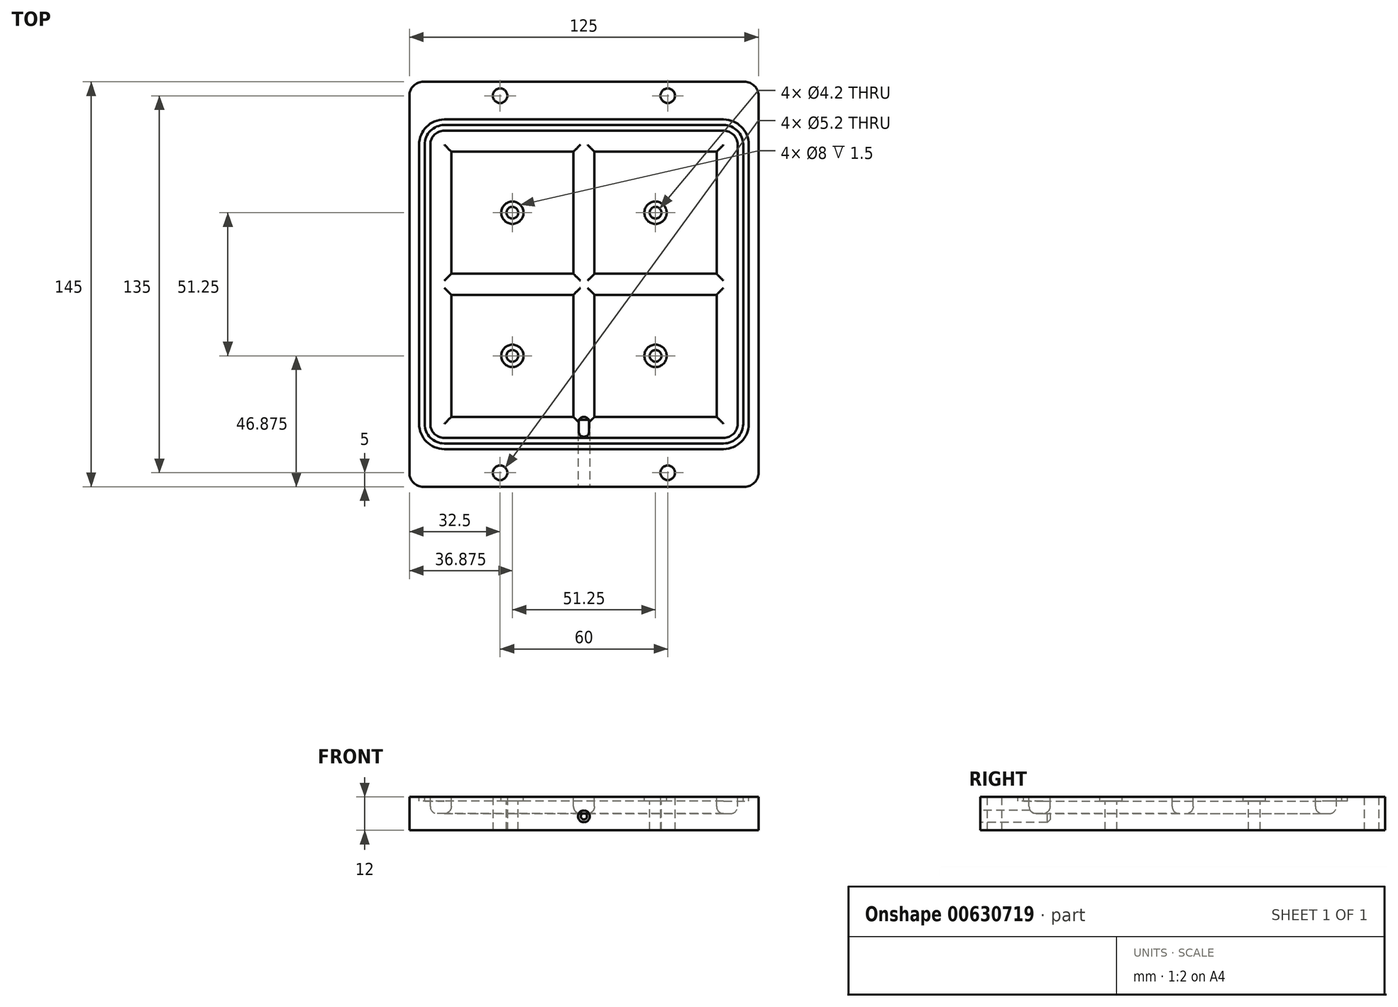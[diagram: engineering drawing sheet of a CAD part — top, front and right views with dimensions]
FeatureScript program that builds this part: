
annotation { "Feature Type Name" : "Feature", "Feature Type Description" : "" }
export const myFeature = defineFeature(function(context is Context, id is Id, definition is map)
    precondition{}
    {
        {
            var Q0;
            Q0=qCreatedBy(makeId("Top.planeOp"),FACE);
            var sketch = newSketch(context, id + "F0", { "sketchPlane" : qUnion([Q0])});
            skLineSegment(sketch, "E0.bottom", {"start": v(52.5, -62.5) * mm, "end": v(-52.5, -62.5) * mm, "construction": true});
            skLineSegment(sketch, "E0.top", {"start": v(52.5, 62.5) * mm, "end": v(-52.5, 62.5) * mm, "construction": true});
            skLineSegment(sketch, "E0.left", {"start": v(62.5, -52.5) * mm, "end": v(62.5, 52.5) * mm, "construction": true});
            skLineSegment(sketch, "E0.right", {"start": v(-62.5, -52.5) * mm, "end": v(-62.5, 52.5) * mm, "construction": true});
            skPoint(sketch, "E0.middle", {"position": v(0, 0) * mm});
            skPoint(sketch, "E1.visualSharp", {"position": v(-62.5, 62.5) * mm});
            skArc(sketch, "E1.filletArc", {"start": v(-52.5, 62.5) * mm, "mid": v(-59.57, 59.57) * mm, "end": v(-62.5, 52.5) * mm, "construction": true});
            skPoint(sketch, "E2.visualSharp", {"position": v(62.5, 62.5) * mm});
            skArc(sketch, "E2.filletArc", {"start": v(62.5, 52.5) * mm, "mid": v(59.57, 59.57) * mm, "end": v(52.5, 62.5) * mm, "construction": true});
            skPoint(sketch, "E3.visualSharp", {"position": v(62.5, -62.5) * mm});
            skArc(sketch, "E3.filletArc", {"start": v(52.5, -62.5) * mm, "mid": v(59.57, -59.57) * mm, "end": v(62.5, -52.5) * mm, "construction": true});
            skPoint(sketch, "E4.visualSharp", {"position": v(-62.5, -62.5) * mm});
            skArc(sketch, "E4.filletArc", {"start": v(-62.5, -52.5) * mm, "mid": v(-59.57, -59.57) * mm, "end": v(-52.5, -62.5) * mm, "construction": true});
            skSolve(sketch);
        }
        {
            var Q0;
            Q0=qCreatedBy(makeId("Top.planeOp"),FACE);
            var sketch = newSketch(context, id + "F1", { "sketchPlane" : qUnion([Q0])});
            skLineSegment(sketch, "E5.bottom", {"start": v(57.5, -72.5) * mm, "end": v(-57.5, -72.5) * mm});
            skLineSegment(sketch, "E5.top", {"start": v(57.5, 72.5) * mm, "end": v(-57.5, 72.5) * mm});
            skLineSegment(sketch, "E5.left", {"start": v(62.5, -67.5) * mm, "end": v(62.5, 67.5) * mm});
            skLineSegment(sketch, "E5.right", {"start": v(-62.5, -67.5) * mm, "end": v(-62.5, 67.5) * mm});
            skPoint(sketch, "E5.middle", {"position": v(0, 0) * mm});
            skPoint(sketch, "E6.visualSharp", {"position": v(-62.5, 72.5) * mm});
            skArc(sketch, "E6.filletArc", {"start": v(-57.5, 72.5) * mm, "mid": v(-61.04, 71.04) * mm, "end": v(-62.5, 67.5) * mm});
            skPoint(sketch, "E7.visualSharp", {"position": v(62.5, 72.5) * mm});
            skArc(sketch, "E7.filletArc", {"start": v(62.5, 67.5) * mm, "mid": v(61.04, 71.04) * mm, "end": v(57.5, 72.5) * mm});
            skPoint(sketch, "E8.visualSharp", {"position": v(62.5, -72.5) * mm});
            skArc(sketch, "E8.filletArc", {"start": v(57.5, -72.5) * mm, "mid": v(61.04, -71.04) * mm, "end": v(62.5, -67.5) * mm});
            skPoint(sketch, "E9.visualSharp", {"position": v(-62.5, -72.5) * mm});
            skArc(sketch, "E9.filletArc", {"start": v(-62.5, -67.5) * mm, "mid": v(-61.04, -71.04) * mm, "end": v(-57.5, -72.5) * mm});
            skLineSegment(sketch, "E10", {"start": v(-62.5, 67.5) * mm, "end": v(52.45, 67.5) * mm, "construction": true});
            skLineSegment(sketch, "E11", {"start": v(-48.85, -67.5) * mm, "end": v(50.9, -67.5) * mm, "construction": true});
            skCircle(sketch, "E12", {"center": v(-30, 67.5) * mm, "radius": 2.6 * mm});
            skCircle(sketch, "E13", {"center": v(30, 67.5) * mm, "radius": 2.6 * mm});
            skCircle(sketch, "E14", {"center": v(-30, -67.5) * mm, "radius": 2.6 * mm});
            skCircle(sketch, "E15", {"center": v(30, -67.5) * mm, "radius": 2.6 * mm});
            skSolve(sketch);
        }
        {
            var Q0;
            Q0=makeQuery(id+"F1.imprint","IMPRINT",FACE,{"disambiguationData":[TD([[makeQuery(id+"F1.imprint","IMPRINT",EDGE,{"derivedFrom":sQuery(id+"F1.wireOp",EDGE,"E5.bottom")}),-1.0]])]});
            extrude(context, id + "F2", {"entities" : qUnion([Q0]), "depth" : 12 * mm, "offsetDistance" : 25 * mm});
        }
        {
            var Q0;
            Q0=makeQuery(id+"F2.opExtrude","CAP_FACE",FACE,{"disambiguationData":[OSD([sQuery(id+"F1.wireOp",EDGE,"E5.bottom"),sQuery(id+"F1.wireOp",EDGE,"E5.top"),sQuery(id+"F1.wireOp",EDGE,"E5.left"),sQuery(id+"F1.wireOp",EDGE,"E5.right"),sQuery(id+"F1.wireOp",EDGE,"E6.filletArc"),sQuery(id+"F1.wireOp",EDGE,"E7.filletArc"),sQuery(id+"F1.wireOp",EDGE,"E8.filletArc"),sQuery(id+"F1.wireOp",EDGE,"E9.filletArc"),sQuery(id+"F1.wireOp",EDGE,"E12"),sQuery(id+"F1.wireOp",EDGE,"E13"),sQuery(id+"F1.wireOp",EDGE,"E14"),sQuery(id+"F1.wireOp",EDGE,"E15")])],"isStart":false});
            var sketch = newSketch(context, id + "F3", { "sketchPlane" : qUnion([Q0])});
            skLineSegment(sketch, "E16.bottom", {"start": v(50, -55) * mm, "end": v(-50, -55) * mm});
            skLineSegment(sketch, "E16.top", {"start": v(50, 55) * mm, "end": v(-50, 55) * mm});
            skLineSegment(sketch, "E16.left", {"start": v(55, -50) * mm, "end": v(55, 50) * mm});
            skLineSegment(sketch, "E16.right", {"start": v(-55, -50) * mm, "end": v(-55, 50) * mm});
            skPoint(sketch, "E16.middle", {"position": v(0, 0) * mm});
            skPoint(sketch, "E17.visualSharp", {"position": v(-55, 55) * mm});
            skArc(sketch, "E17.filletArc", {"start": v(-50, 55) * mm, "mid": v(-53.54, 53.54) * mm, "end": v(-55, 50) * mm});
            skPoint(sketch, "E18.visualSharp", {"position": v(55, 55) * mm});
            skArc(sketch, "E18.filletArc", {"start": v(55, 50) * mm, "mid": v(53.54, 53.54) * mm, "end": v(50, 55) * mm});
            skPoint(sketch, "E19.visualSharp", {"position": v(55, -55) * mm});
            skArc(sketch, "E19.filletArc", {"start": v(50, -55) * mm, "mid": v(53.54, -53.54) * mm, "end": v(55, -50) * mm});
            skPoint(sketch, "E20.visualSharp", {"position": v(-55, -55) * mm});
            skArc(sketch, "E20.filletArc", {"start": v(-55, -50) * mm, "mid": v(-53.54, -53.54) * mm, "end": v(-50, -55) * mm});
            skLineSegment(sketch, "E21.0", {"start": v(-47.5, -47.5) * mm, "end": v(-47.5, -3.75) * mm});
            skLineSegment(sketch, "E21.1", {"start": v(47.5, -47.5) * mm, "end": v(3.75, -47.5) * mm});
            skLineSegment(sketch, "E21.2", {"start": v(47.5, -47.5) * mm, "end": v(47.5, -3.75) * mm});
            skLineSegment(sketch, "E21.3", {"start": v(47.5, 47.5) * mm, "end": v(3.75, 47.5) * mm});
            skLineSegment(sketch, "E22.0.left", {"start": v(-47.5, 3.75) * mm, "end": v(-3.75, 3.75) * mm});
            skLineSegment(sketch, "E22.0.right", {"start": v(-47.5, -3.75) * mm, "end": v(-3.75, -3.75) * mm});
            skLineSegment(sketch, "E23.0.left", {"start": v(3.75, 47.5) * mm, "end": v(3.75, 3.75) * mm});
            skLineSegment(sketch, "E23.0.right", {"start": v(-3.75, 47.5) * mm, "end": v(-3.75, 3.75) * mm});
            skLineSegment(sketch, "E24.trimOffspring", {"start": v(-3.75, 47.5) * mm, "end": v(-47.5, 47.5) * mm});
            skLineSegment(sketch, "E25.trimOffspring", {"start": v(3.75, 3.75) * mm, "end": v(47.5, 3.75) * mm});
            skLineSegment(sketch, "E26.trimOffspring", {"start": v(3.75, -3.75) * mm, "end": v(3.75, -47.5) * mm});
            skLineSegment(sketch, "E27.trimOffspring", {"start": v(3.75, -3.75) * mm, "end": v(47.5, -3.75) * mm});
            skLineSegment(sketch, "E28.trimOffspring", {"start": v(-3.75, -3.75) * mm, "end": v(-3.75, -47.5) * mm});
            skPoint(sketch, "E22.0.startCap.center.orphan", {"position": v(-47.5, 0) * mm});
            skLineSegment(sketch, "E29.trimOffspring", {"start": v(-47.5, 3.75) * mm, "end": v(-47.5, 47.5) * mm});
            skLineSegment(sketch, "E30.trimOffspring", {"start": v(47.5, 3.75) * mm, "end": v(47.5, 47.5) * mm});
            skPoint(sketch, "E22.0.endCap.center.orphan", {"position": v(47.5, 0) * mm});
            skPoint(sketch, "E23.0.endCap.center.orphan", {"position": v(0, -47.5) * mm});
            skLineSegment(sketch, "E31.trimOffspring", {"start": v(-3.75, -47.5) * mm, "end": v(-47.5, -47.5) * mm});
            skSolve(sketch);
        }
        {
            var Q0;
            Q0 = qSketchRegion(id + "F3", true);
            extrude(context, id + "F4", {"entities" : qUnion([Q0]), "operationType" : NewBodyOperationType.REMOVE, "oppositeDirection" : true, "depth" : 6 * mm, "offsetDistance" : 25 * mm});
        }
        {
            var Q0;
            Q0=makeQuery(id+"F4.boolean.opBoolean","COPY",FACE,{"derivedFrom":makeQuery(id+"F4.opExtrude","CAP_FACE",FACE,{"disambiguationData":[OSD([sQuery(id+"F3.wireOp",EDGE,"E16.bottom"),sQuery(id+"F3.wireOp",EDGE,"E16.top"),sQuery(id+"F3.wireOp",EDGE,"E16.left"),sQuery(id+"F3.wireOp",EDGE,"E16.right"),sQuery(id+"F3.wireOp",EDGE,"E17.filletArc"),sQuery(id+"F3.wireOp",EDGE,"E18.filletArc"),sQuery(id+"F3.wireOp",EDGE,"E19.filletArc"),sQuery(id+"F3.wireOp",EDGE,"E20.filletArc"),sQuery(id+"F3.wireOp",EDGE,"E21.0"),sQuery(id+"F3.wireOp",EDGE,"E21.1"),sQuery(id+"F3.wireOp",EDGE,"E21.2"),sQuery(id+"F3.wireOp",EDGE,"E21.3"),sQuery(id+"F3.wireOp",EDGE,"E22.0.left"),sQuery(id+"F3.wireOp",EDGE,"E22.0.right"),sQuery(id+"F3.wireOp",EDGE,"E23.0.left"),sQuery(id+"F3.wireOp",EDGE,"E23.0.right"),sQuery(id+"F3.wireOp",EDGE,"E24.trimOffspring"),sQuery(id+"F3.wireOp",EDGE,"E25.trimOffspring"),sQuery(id+"F3.wireOp",EDGE,"E26.trimOffspring"),sQuery(id+"F3.wireOp",EDGE,"E27.trimOffspring"),sQuery(id+"F3.wireOp",EDGE,"E28.trimOffspring"),sQuery(id+"F3.wireOp",EDGE,"E29.trimOffspring"),sQuery(id+"F3.wireOp",EDGE,"E30.trimOffspring"),sQuery(id+"F3.wireOp",EDGE,"E31.trimOffspring")])],"isStart":false})});
            fillet(context, id + "F5", {"entities" : qUnion([Q0]), "radius" : 2.5 * mm, "tangentPropagation" : true, "allowEdgeOverflow" : false});
        }
        {
            var Q0;
            Q0=makeQuery(id+"F4.boolean.opBoolean","SPLIT",FACE,{"disambiguationData":[TD([makeQuery(id+"F4.opExtrude","SWEPT_FACE",FACE,{"disambiguationData":[OSD([sQuery(id+"F3.wireOp",EDGE,"E22.0.left")])]})])],"derivedFrom":makeQuery(id+"F2.opExtrude","CAP_FACE",FACE,{"disambiguationData":[OSD([sQuery(id+"F1.wireOp",EDGE,"E5.bottom"),sQuery(id+"F1.wireOp",EDGE,"E5.top"),sQuery(id+"F1.wireOp",EDGE,"E5.left"),sQuery(id+"F1.wireOp",EDGE,"E5.right"),sQuery(id+"F1.wireOp",EDGE,"E6.filletArc"),sQuery(id+"F1.wireOp",EDGE,"E7.filletArc"),sQuery(id+"F1.wireOp",EDGE,"E8.filletArc"),sQuery(id+"F1.wireOp",EDGE,"E9.filletArc"),sQuery(id+"F1.wireOp",EDGE,"E12"),sQuery(id+"F1.wireOp",EDGE,"E13"),sQuery(id+"F1.wireOp",EDGE,"E14"),sQuery(id+"F1.wireOp",EDGE,"E15")])],"isStart":false})});
            var sketch = newSketch(context, id + "F6", { "sketchPlane" : qUnion([Q0])});
            skCircle(sketch, "E32", {"center": v(-25.62, 25.62) * mm, "radius": 2.1 * mm});
            skLineSegment(sketch, "E33.bottom", {"start": v(-25.62, 25.62) * mm, "end": v(25.62, 25.62) * mm, "construction": true});
            skLineSegment(sketch, "E33.top", {"start": v(-25.62, -25.62) * mm, "end": v(25.62, -25.62) * mm, "construction": true});
            skLineSegment(sketch, "E33.left", {"start": v(-25.62, 25.62) * mm, "end": v(-25.62, -25.62) * mm, "construction": true});
            skLineSegment(sketch, "E33.right", {"start": v(25.62, 25.62) * mm, "end": v(25.62, -25.62) * mm, "construction": true});
            skPoint(sketch, "E33.middle", {"position": v(0, 0) * mm});
            skCircle(sketch, "E34", {"center": v(25.62, 25.62) * mm, "radius": 2.1 * mm});
            skCircle(sketch, "E35", {"center": v(25.62, -25.62) * mm, "radius": 2.1 * mm});
            skCircle(sketch, "E36", {"center": v(-25.62, -25.62) * mm, "radius": 2.1 * mm});
            skSolve(sketch);
        }
        {
            var Q0;
            Q0 = qSketchRegion(id + "F6", true);
            extrude(context, id + "F7", {"entities" : qUnion([Q0]), "operationType" : NewBodyOperationType.REMOVE, "oppositeDirection" : true, "depth" : 25 * mm, "offsetDistance" : 25 * mm});
        }
        {
            var Q0;
            Q0=makeQuery(id+"F4.boolean.opBoolean","SPLIT",FACE,{"disambiguationData":[TD([makeQuery(id+"F4.opExtrude","SWEPT_FACE",FACE,{"disambiguationData":[OSD([sQuery(id+"F3.wireOp",EDGE,"E22.0.left")])]})])],"derivedFrom":makeQuery(id+"F2.opExtrude","CAP_FACE",FACE,{"disambiguationData":[OSD([sQuery(id+"F1.wireOp",EDGE,"E5.bottom"),sQuery(id+"F1.wireOp",EDGE,"E5.top"),sQuery(id+"F1.wireOp",EDGE,"E5.left"),sQuery(id+"F1.wireOp",EDGE,"E5.right"),sQuery(id+"F1.wireOp",EDGE,"E6.filletArc"),sQuery(id+"F1.wireOp",EDGE,"E7.filletArc"),sQuery(id+"F1.wireOp",EDGE,"E8.filletArc"),sQuery(id+"F1.wireOp",EDGE,"E9.filletArc"),sQuery(id+"F1.wireOp",EDGE,"E12"),sQuery(id+"F1.wireOp",EDGE,"E13"),sQuery(id+"F1.wireOp",EDGE,"E14"),sQuery(id+"F1.wireOp",EDGE,"E15")])],"isStart":false})});
            var sketch = newSketch(context, id + "F8", { "sketchPlane" : qUnion([Q0])});
            skCircle(sketch, "E37", {"center": v(-25.62, 25.62) * mm, "radius": 4 * mm});
            skCircle(sketch, "E38.0.1.0", {"center": v(-25.62, -25.63) * mm, "radius": 4 * mm});
            skCircle(sketch, "E38.1.0.0", {"center": v(25.63, 25.62) * mm, "radius": 4 * mm});
            skCircle(sketch, "E38.1.1.0", {"center": v(25.63, -25.63) * mm, "radius": 4 * mm});
            skLineSegment(sketch, "E38.direction1", {"start": v(-25.62, 25.62) * mm, "end": v(25.63, 25.62) * mm, "construction": true});
            skLineSegment(sketch, "E38.direction2", {"start": v(-25.62, 25.62) * mm, "end": v(-25.62, -25.63) * mm, "construction": true});
            skSolve(sketch);
        }
        {
            var Q0;
            {var subQ0=sQuery(id+"F1.wireOp",EDGE,"E12");var subQ1=sQuery(id+"F1.wireOp",EDGE,"E9.filletArc");var subQ2=sQuery(id+"F1.wireOp",EDGE,"E8.filletArc");var subQ3=sQuery(id+"F1.wireOp",EDGE,"E7.filletArc");var subQ4=sQuery(id+"F1.wireOp",EDGE,"E6.filletArc");var subQ5=sQuery(id+"F1.wireOp",EDGE,"E13");var subQ6=sQuery(id+"F1.wireOp",EDGE,"E5.bottom");var subQ7=sQuery(id+"F1.wireOp",EDGE,"E5.right");var subQ8=sQuery(id+"F1.wireOp",EDGE,"E5.top");var subQ9=sQuery(id+"F1.wireOp",EDGE,"E5.left");var subQ10=sQuery(id+"F1.wireOp",EDGE,"E14");var subQ11=sQuery(id+"F1.wireOp",EDGE,"E15");Q0=makeQuery(id+"F4.boolean.opBoolean","SPLIT",FACE,{"disambiguationData":[TD([makeQuery(id+"F2.opExtrude","SWEPT_FACE",FACE,{"disambiguationData":[OSD([subQ6])]})])],"derivedFrom":makeQuery(id+"F2.opExtrude","CAP_FACE",FACE,{"disambiguationData":[OSD([subQ6,subQ8,subQ9,subQ7,subQ4,subQ3,subQ2,subQ1,subQ0,subQ5,subQ10,subQ11])],"isStart":false})});}
            var sketch = newSketch(context, id + "F9", { "sketchPlane" : qUnion([Q0])});
            skArc(sketch, "E39.0", {"start": v(-50, 55) * mm, "mid": v(-53.54, 53.54) * mm, "end": v(-55, 50) * mm, "construction": true});
            skLineSegment(sketch, "E40.0", {"start": v(50, 55) * mm, "end": v(-50, 55) * mm, "construction": true});
            skLineSegment(sketch, "E41.0", {"start": v(-55, -50) * mm, "end": v(-55, 50) * mm, "construction": true});
            skPoint(sketch, "E42.0", {"position": v(53.54, 53.54) * mm});
            skArc(sketch, "E43.0", {"start": v(55, 50) * mm, "mid": v(53.54, 53.54) * mm, "end": v(50, 55) * mm, "construction": true});
            skLineSegment(sketch, "E44.0", {"start": v(55, -50) * mm, "end": v(55, 50) * mm, "construction": true});
            skArc(sketch, "E45.0", {"start": v(50, -55) * mm, "mid": v(53.54, -53.54) * mm, "end": v(55, -50) * mm, "construction": true});
            skLineSegment(sketch, "E46.0", {"start": v(50, -55) * mm, "end": v(-50, -55) * mm, "construction": true});
            skArc(sketch, "E47.0", {"start": v(-55, -50) * mm, "mid": v(-53.54, -53.54) * mm, "end": v(-50, -55) * mm, "construction": true});
            skArc(sketch, "E48.0", {"start": v(50, -57) * mm, "mid": v(54.95, -54.95) * mm, "end": v(57, -50) * mm});
            skLineSegment(sketch, "E48.1", {"start": v(50, -57) * mm, "end": v(-50, -57) * mm});
            skLineSegment(sketch, "E48.2", {"start": v(57, -50) * mm, "end": v(57, 50) * mm});
            skArc(sketch, "E48.3", {"start": v(-57, -50) * mm, "mid": v(-54.95, -54.95) * mm, "end": v(-50, -57) * mm});
            skArc(sketch, "E48.4", {"start": v(57, 50) * mm, "mid": v(54.95, 54.95) * mm, "end": v(50, 57) * mm});
            skLineSegment(sketch, "E48.5", {"start": v(50, 57) * mm, "end": v(-50, 57) * mm});
            skArc(sketch, "E48.6", {"start": v(-50, 57) * mm, "mid": v(-54.95, 54.95) * mm, "end": v(-57, 50) * mm});
            skLineSegment(sketch, "E48.7", {"start": v(-57, -50) * mm, "end": v(-57, 50) * mm});
            skArc(sketch, "E49.0", {"start": v(-50, 59) * mm, "mid": v(-56.36, 56.36) * mm, "end": v(-59, 50) * mm});
            skLineSegment(sketch, "E49.1", {"start": v(50, 59) * mm, "end": v(-50, 59) * mm});
            skArc(sketch, "E50.0", {"start": v(59, 50) * mm, "mid": v(56.36, 56.36) * mm, "end": v(50, 59) * mm});
            skLineSegment(sketch, "E50.1", {"start": v(59, -50) * mm, "end": v(59, 50) * mm});
            skLineSegment(sketch, "E50.2", {"start": v(-59, -50) * mm, "end": v(-59, 50) * mm});
            skArc(sketch, "E50.3", {"start": v(-59, -50) * mm, "mid": v(-56.36, -56.36) * mm, "end": v(-50, -59) * mm});
            skLineSegment(sketch, "E50.4", {"start": v(50, -59) * mm, "end": v(-50, -59) * mm});
            skArc(sketch, "E50.5", {"start": v(50, -59) * mm, "mid": v(56.36, -56.36) * mm, "end": v(59, -50) * mm});
            skSolve(sketch);
        }
        {
            var Q0;
            Q0 = qSketchRegion(id + "F9", true);
            extrude(context, id + "F10", {"entities" : qUnion([Q0]), "operationType" : NewBodyOperationType.REMOVE, "oppositeDirection" : true, "depth" : 1.5 * mm, "offsetDistance" : 25 * mm});
        }
        {
            var Q0;
            Q0 = qSketchRegion(id + "F8", true);
            extrude(context, id + "F11", {"entities" : qUnion([Q0]), "operationType" : NewBodyOperationType.REMOVE, "oppositeDirection" : true, "depth" : 1.5 * mm, "offsetDistance" : 25 * mm});
        }
        {
            var Q0;
            Q0=makeQuery(id+"F2.opExtrude","SWEPT_FACE",FACE,{"disambiguationData":[OSD([sQuery(id+"F1.wireOp",EDGE,"E5.bottom")])]});
            var sketch = newSketch(context, id + "F12", { "sketchPlane" : qUnion([Q0])});
            skCircle(sketch, "E51", {"center": v(0, 5) * mm, "radius": 2.1 * mm});
            skSolve(sketch);
        }
        {
            var Q0;
            Q0=makeQuery(id+"F12.imprint","IMPRINT",FACE,{"disambiguationData":[TD([[makeQuery(id+"F12.imprint","IMPRINT",EDGE,{"derivedFrom":sQuery(id+"F12.wireOp",EDGE,"E51")}),1.0]])]});
            extrude(context, id + "F13", {"entities" : qUnion([Q0]), "operationType" : NewBodyOperationType.REMOVE, "oppositeDirection" : true, "depth" : 25 * mm, "offsetDistance" : 25 * mm});
        }
        {
            var Q0;
            Q0=makeQuery(id+"F13.boolean.opBoolean","COPY",EDGE,{"derivedFrom":makeQuery(id+"F13.opExtrude","CAP_EDGE",EDGE,{"disambiguationData":[OSD([sQuery(id+"F12.wireOp",EDGE,"E51")])],"isStart":false})});
            chamfer(context, id + "F14", {"entities" : qUnion([Q0]), "width" : 1 * mm, "tangentPropagation" : true});
        }
    });
